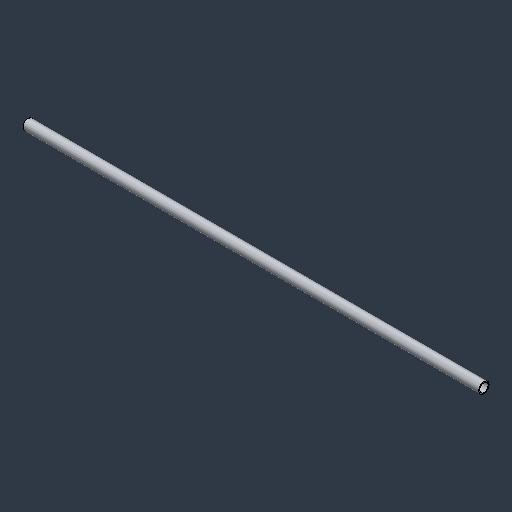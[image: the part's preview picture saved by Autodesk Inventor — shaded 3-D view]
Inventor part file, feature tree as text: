
AUTODESK INVENTOR PART (.ipt)
format: ipt  version: 2024.3 (Build 283343000, 343)  size: 96,256 bytes
history: native  units: mm (DEFAULTED — no unit token found)
features: mirror x1
ambient origin geometry x8: Origin, YZ Plane, XZ Plane, XY Plane, X Axis, Y Axis, Z Axis, Center Point
bodies: Solid1 (feature_tree)
feature tree (1):
  mirror  "Mirror1"
